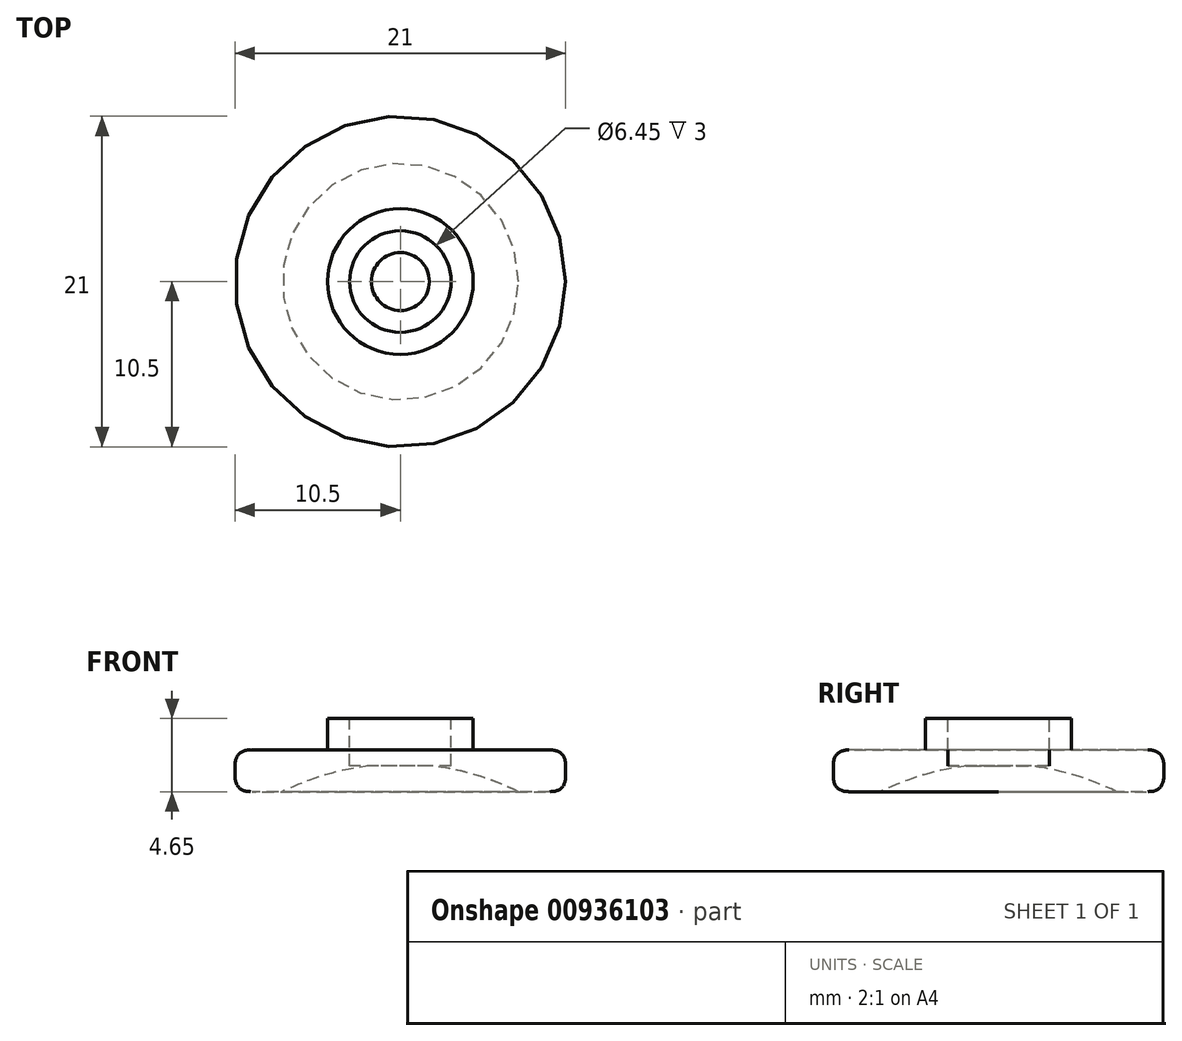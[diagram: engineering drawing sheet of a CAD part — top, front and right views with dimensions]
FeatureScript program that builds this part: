
annotation { "Feature Type Name" : "Feature", "Feature Type Description" : "" }
export const myFeature = defineFeature(function(context is Context, id is Id, definition is map)
    precondition{}
    {
        {
            var Q0;
            Q0=qCreatedBy(makeId("Top.planeOp"),FACE);
            var sketch = newSketch(context, id + "F0", { "sketchPlane" : qUnion([Q0])});
            skCircle(sketch, "E0", {"center": v(0, 0) * mm, "radius": 10.5 * mm});
            skSolve(sketch);
        }
        {
            var Q0;
            Q0=makeQuery(id+"F0.imprint","IMPRINT",FACE,{"disambiguationData":[TD([[makeQuery(id+"F0.imprint","IMPRINT",EDGE,{"derivedFrom":sQuery(id+"F0.wireOp",EDGE,"E0")}),1.0]])]});
            extrude(context, id + "F1", {"entities" : qUnion([Q0]), "depth" : 2.65 * mm, "offsetDistance" : 25 * mm});
        }
        {
            var Q0;
            Q0=makeQuery(id+"F1.opExtrude","CAP_FACE",FACE,{"disambiguationData":[OSD([sQuery(id+"F0.wireOp",EDGE,"E0")])],"isStart":false});
            var sketch = newSketch(context, id + "F2", { "sketchPlane" : qUnion([Q0])});
            skCircle(sketch, "E1", {"center": v(0, 0) * mm, "radius": 4.62 * mm});
            skSolve(sketch);
        }
        {
            var Q0;
            Q0=qSketchRegion(id+"F2",true);
            extrude(context, id + "F3", {"entities" : qUnion([Q0]), "operationType" : NewBodyOperationType.ADD, "depth" : 2 * mm, "offsetDistance" : 25 * mm});
        }
        {
            var Q0;
            Q0=makeQuery(id+"F3.opExtrude","CAP_FACE",FACE,{"disambiguationData":[OSD([sQuery(id+"F2.wireOp",EDGE,"E1")])],"isStart":false});
            var sketch = newSketch(context, id + "F4", { "sketchPlane" : qUnion([Q0])});
            skCircle(sketch, "E2", {"center": v(0, 0) * mm, "radius": 3.22 * mm});
            skSolve(sketch);
        }
        {
            var Q0;
            Q0=qCreatedBy(makeId("Front.planeOp"),FACE);
            var sketch = newSketch(context, id + "F5", { "sketchPlane" : qUnion([Q0])});
            skLineSegment(sketch, "E3", {"start": v(0, 0) * mm, "end": v(-7.5, 0) * mm});
            skLineSegment(sketch, "E4", {"start": v(0, 0) * mm, "end": v(0, 1.75) * mm});
            skArc(sketch, "E5", {"start": v(0, 1.75) * mm, "mid": v(-3.85, 1.3) * mm, "end": v(-7.5, 0) * mm});
            skSolve(sketch);
        }
        {
            var Q0;
            Q0=qSketchRegion(id+"F5",true);
            var Q1;
            Q1=sQuery(id+"F5.wireOp",EDGE,"E4");
            revolve(context, id + "F6", {"operationType" : NewBodyOperationType.REMOVE, "surfaceOperationType" : NewSurfaceOperationType.NEW, "entities" : qUnion([Q0]), "axis" : qUnion([Q1]), "revolveType" : RevolveType.FULL, "oppositeDirection" : true});
        }
        {
            var Q0;
            Q0=makeQuery(id+"F1.opExtrude","CAP_EDGE",EDGE,{"disambiguationData":[OSD([sQuery(id+"F0.wireOp",EDGE,"E0")])],"isStart":true});
            fillet(context, id + "F7", {"entities" : qUnion([Q0]), "radius" : 1 * mm, "rho" : .5, "crossSection" : FilletCrossSection.CONIC, "allowEdgeOverflow" : false});
        }
        {
            var Q0;
            Q0=makeQuery(id+"F1.opExtrude","CAP_EDGE",EDGE,{"disambiguationData":[OSD([sQuery(id+"F0.wireOp",EDGE,"E0")])],"isStart":false});
            fillet(context, id + "F8", {"entities" : qUnion([Q0]), "radius" : 1 * mm, "rho" : 0.5, "crossSection" : FilletCrossSection.CONIC, "allowEdgeOverflow" : false});
        }
        {
            var Q0;
            Q0=makeQuery(id+"F4.imprint","IMPRINT",FACE,{"disambiguationData":[TD([[makeQuery(id+"F4.imprint","IMPRINT",EDGE,{"derivedFrom":sQuery(id+"F4.wireOp",EDGE,"E2")}),1.0]])]});
            extrude(context, id + "F9", {"entities" : qUnion([Q0]), "operationType" : NewBodyOperationType.REMOVE, "oppositeDirection" : true, "depth" : 3 * mm, "offsetDistance" : 25 * mm});
        }
    });
